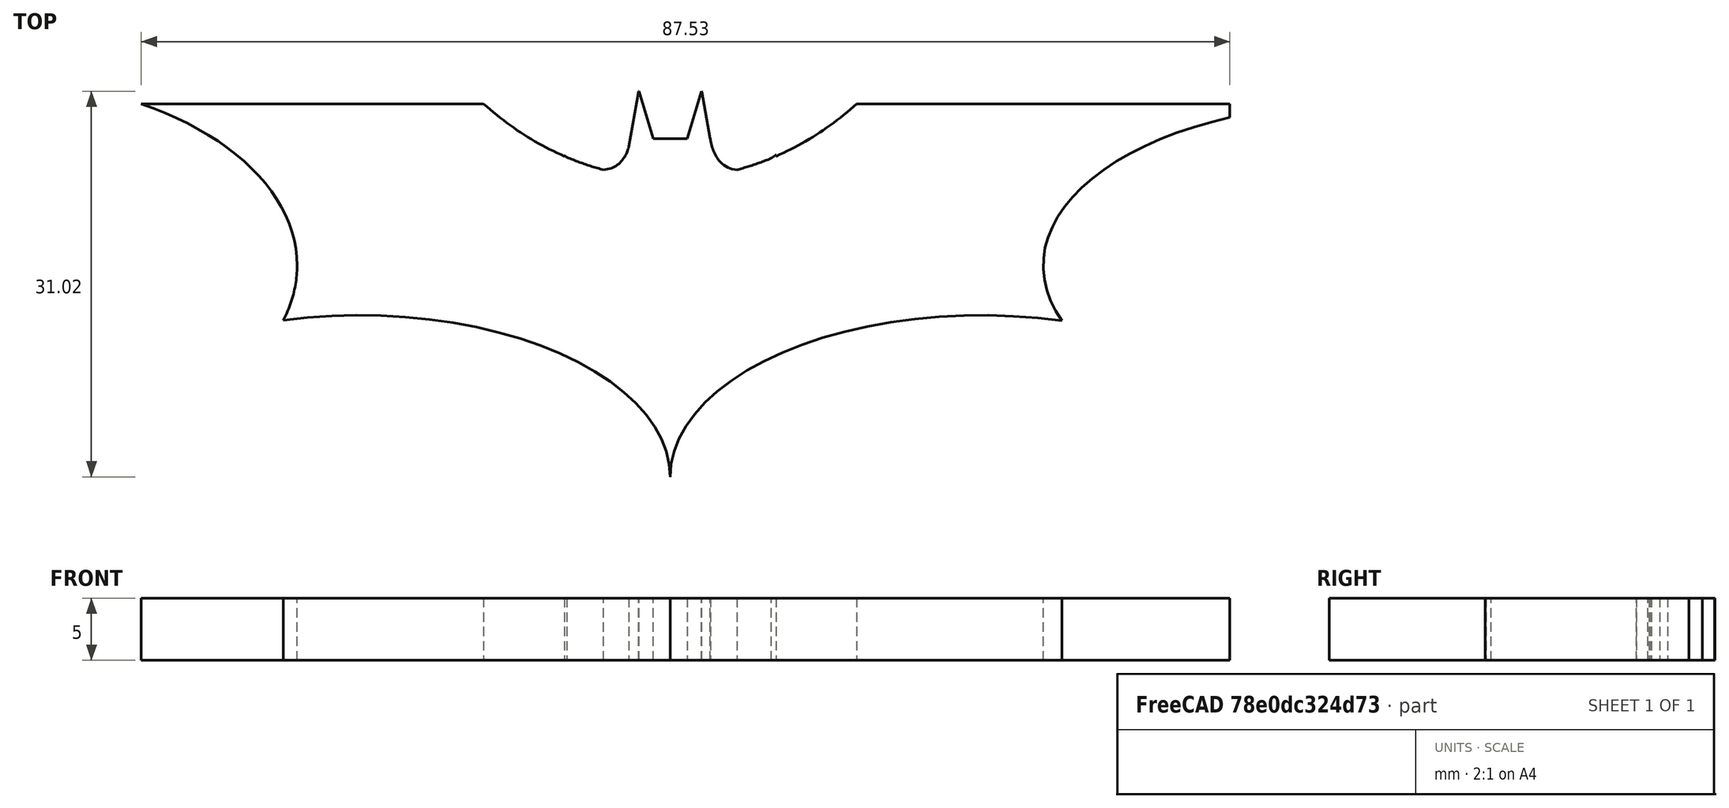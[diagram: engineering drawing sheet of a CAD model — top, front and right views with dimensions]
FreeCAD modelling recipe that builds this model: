
FCSTD DOCUMENT  (FreeCAD 0.16R6706 (Git))
Label: Batman FINAL
License: All rights reserved
LicenseURL: http://en.wikipedia.org/wiki/All_rights_reserved
objects: Part::Feature×13, Part::Extrusion×9, Part::Cut×7, Part::Line×5, Part::Ellipse×3, Part::Box×2, Part::MultiFuse×2
note: 41 computed .brp shape members not serialized (recipe doc carries the construction recipe); baked Part::Feature solids carry a one-line shape summary decoded from their .brp

FEATURE [Part::Box] Box  label="Cubo"
  Height = 5
  Length = 90
  Width = 30
FEATURE [Part::Feature] Face
  shape: bbox 71 x 28.35 x 2e-07 mm, 1 faces, 0 solids (baked)
FEATURE [Part::Extrusion] Extrude  label="Elipse Abajo 1"
  Base = -> Face
  Dir = (0,0,5)
  Placement = pos=(20,0,0) rot=(0,0,1;0rad)
  Solid = false
FEATURE [Part::Feature] Face001
  shape: bbox 71 x 28.35 x 2e-07 mm, 1 faces, 0 solids (baked)
FEATURE [Part::Extrusion] Extrude001  label="Elipse Abajo 2"
  Base = -> Face001
  Dir = (0,0,5)
  Placement = pos=(70,0,0) rot=(0,0,1;0rad)
  Solid = false
FEATURE [Part::Feature] Face002
  shape: bbox 71.47 x 32.68 x 2e-07 mm, 1 faces, 0 solids (baked)
FEATURE [Part::Extrusion] Extrude002  label="Elipse Lado Izq"
  Base = -> Face002
  Dir = (0,0,5)
  Placement = pos=(-10,17,0) rot=(0,0,1;0rad)
  Solid = false
FEATURE [Part::Feature] Face003
  shape: bbox 71 x 28.35 x 2e-07 mm, 1 faces, 0 solids (baked)
FEATURE [Part::Extrusion] Extrude003
  Base = -> Face003
  Dir = (0,0,5)
  Placement = pos=(100,17,0) rot=(0,0,1;0rad)
  Solid = false
FEATURE [Part::Cut] Cut
  Base = -> Box
  Tool = -> Extrude002
FEATURE [Part::Cut] Cut001
  Base = -> Cut
  Tool = -> Extrude
FEATURE [Part::Cut] Cut002
  Base = -> Cut001
  Tool = -> Extrude003
FEATURE [Part::Cut] Cut003
  Base = -> Cut002
  Tool = -> Extrude001
FEATURE [Part::Feature] Face004
  Placement = pos=(0,3,0) rot=(0,0,1;0rad)
  shape: bbox 54.52 x 88.54 x 2e-07 mm, 1 faces, 0 solids (baked)
FEATURE [Part::Extrusion] Extrude004
  Base = -> Face004
  Dir = (0,0,5)
  Placement = pos=(0,1,0) rot=(0,0,1;0rad)
  Solid = false
FEATURE [Part::Cut] Cut004  label="Base"
  Base = -> Cut003
  Tool = -> Extrude004
FEATURE [Part::Line] Line  label="Línea"
  Placement = pos=(-0.9,0.1,0) rot=(0,0,-1;0.174533rad)
  X1 = 0
  X2 = 0
  Y1 = 0
  Y2 = 5
  Z1 = 0
  Z2 = 0
FEATURE [Part::Line] Line003  label="Línea003"
  X1 = 0
  X2 = 1.5
  Y1 = 5
  Y2 = 0
  Z1 = 0
  Z2 = 0
FEATURE [Part::Line] Line004  label="Línea004"
  X1 = 1.5
  X2 = 3.5
  Y1 = 0
  Y2 = 0
  Z1 = 0
  Z2 = 0
FEATURE [Part::Line] Line005  label="Línea005"
  X1 = 3.5
  X2 = 5
  Y1 = 0
  Y2 = 5
  Z1 = 0
  Z2 = 0
FEATURE [Part::Line] Line006  label="Línea006"
  Placement = pos=(1,-0.8,0) rot=(0,0,1;0.174533rad)
  X1 = 5
  X2 = 5
  Y1 = 5
  Y2 = 0
  Z1 = 0
  Z2 = 0
FEATURE [Part::Feature] Edge
  shape: bbox 0.03176 x 0.02404 x 2e-07 mm, 0 faces, 0 solids (baked)
FEATURE [Part::Feature] Edge001
  shape: bbox 2.4 x 0.1 x 2e-07 mm, 0 faces, 0 solids (baked)
FEATURE [Part::Feature] Edge002
  shape: bbox 2.424 x 0.06824 x 2e-07 mm, 0 faces, 0 solids (baked)
FEATURE [Part::Feature] Edge003
  shape: bbox 0.0558 x 0.007721 x 2e-07 mm, 0 faces, 0 solids (baked)
FEATURE [Part::Feature] Face005
  Placement = pos=(42.5,26,0) rot=(0,0,1;0rad)
  shape: bbox 3.053 x 5.783 x 2e-07 mm, 1 faces, 0 solids (baked)
FEATURE [Part::Feature] Face006
  Placement = pos=(42.5,26,0) rot=(0,0,1;0rad)
  shape: bbox 3.034 x 5.814 x 2e-07 mm, 1 faces, 0 solids (baked)
FEATURE [Part::Extrusion] Extrude005  label="Cuerno I"
  Base = -> Face006
  Dir = (0,0,5)
  Solid = false
FEATURE [Part::Extrusion] Extrude006  label="Cuerno D"
  Base = -> Face005
  Dir = (0,0,5)
  Solid = false
FEATURE [Part::Box] Box001  label="Cubo001"
  Height = 5
  Length = 17
  Placement = pos=(36.5,22,0) rot=(0,0,1;0rad)
  Width = 5.2
FEATURE [Part::Ellipse] Ellipse  label="Elipse"
  Angle0 = 0
  Angle1 = 360
  MajorRadius = 8
  MinorRadius = 6
FEATURE [Part::Ellipse] Ellipse001  label="Elipse001"
  Angle0 = 0
  Angle1 = 360
  MajorRadius = 8
  MinorRadius = 4
  Placement = pos=(36.4,31.8,6) rot=(0,0,1;2.1293rad)
FEATURE [Part::Ellipse] Ellipse002  label="Elipse002"
  Angle0 = 0
  Angle1 = 360
  MajorRadius = 8
  MinorRadius = 4
  Placement = pos=(53.4,31.95,6) rot=(0,0,1;1.06465rad)
FEATURE [Part::Feature] Face007
  shape: bbox 16.79 x 21.65 x 2e-07 mm, 1 faces, 0 solids (baked)
FEATURE [Part::Feature] Face008
  shape: bbox 16.01 x 22.06 x 2e-07 mm, 1 faces, 0 solids (baked)
FEATURE [Part::Extrusion] Extrude007
  Base = -> Face007
  Dir = (0,0,7)
  Placement = pos=(0,0,-7) rot=(0,0,1;0rad)
  Solid = false
FEATURE [Part::Extrusion] Extrude008
  Base = -> Face008
  Dir = (0,0,7)
  Placement = pos=(0,0,-7) rot=(0,0,1;0rad)
  Solid = false
FEATURE [Part::Cut] Cut005
  Base = -> Box001
  Tool = -> Extrude007
FEATURE [Part::Cut] Cut006  label="Cabesa"
  Base = -> Cut005
  Tool = -> Extrude008
FEATURE [Part::MultiFuse] Fusion
  Shapes = -> [Extrude006,Extrude005,Cut006]
FEATURE [Part::MultiFuse] Fusion001
  Shapes = -> [Fusion,Cut004]
